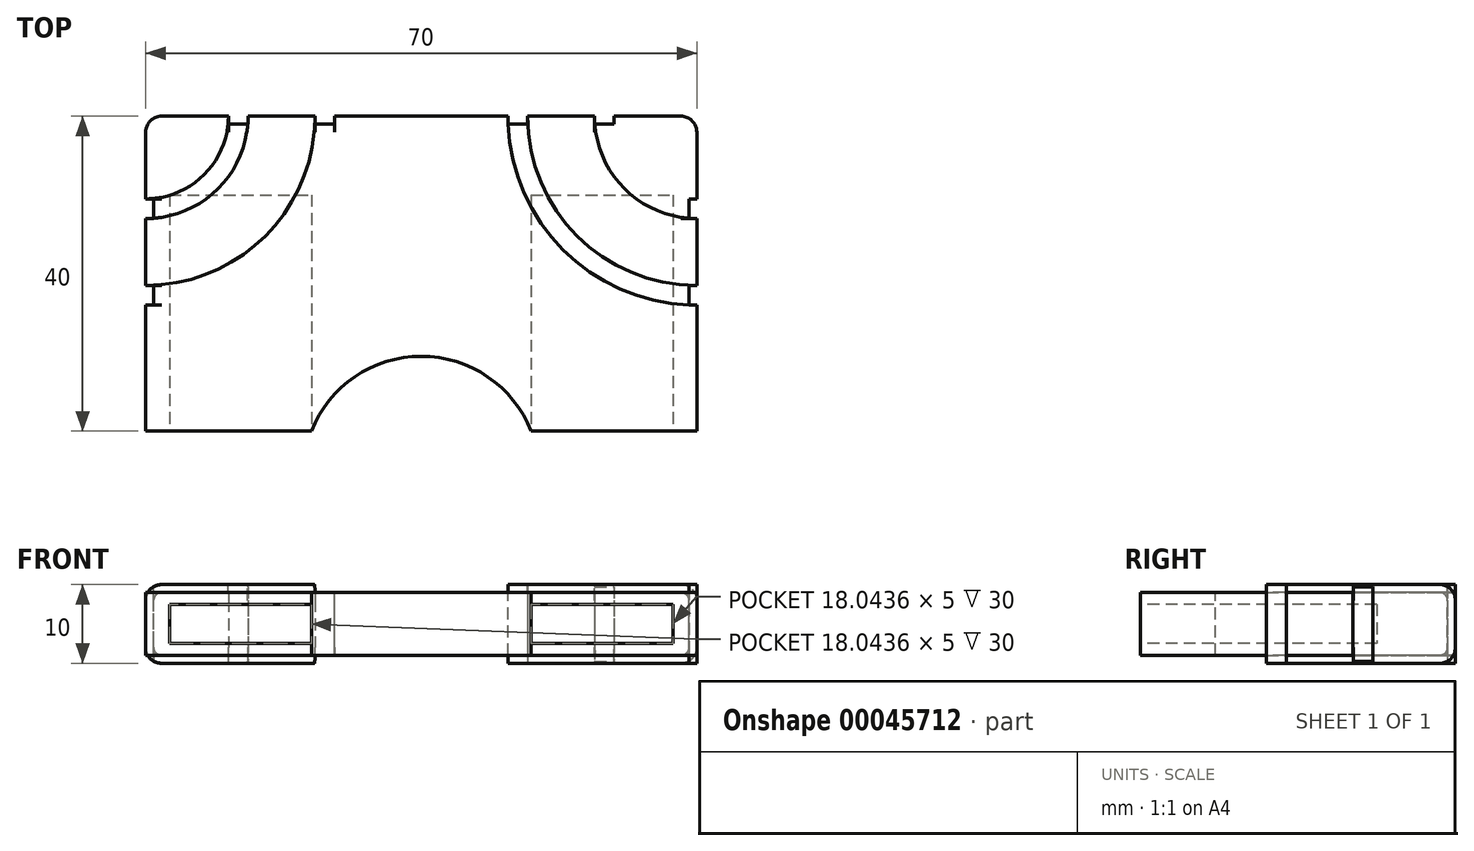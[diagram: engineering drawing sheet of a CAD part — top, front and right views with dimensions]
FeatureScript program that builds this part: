
annotation { "Feature Type Name" : "Feature", "Feature Type Description" : "" }
export const myFeature = defineFeature(function(context is Context, id is Id, definition is map)
    precondition{}
    {
        {
            var Q0;
            Q0=qCreatedBy(makeId("Top.planeOp"),FACE);
            var sketch = newSketch(context, id + "F0", { "sketchPlane" : qUnion([Q0])});
            skLineSegment(sketch, "E0.top", {"start": v(35, 70) * mm, "end": v(-35, 70) * mm});
            skLineSegment(sketch, "E0.left", {"start": v(35, 30) * mm, "end": v(35, 70) * mm});
            skLineSegment(sketch, "E0.right", {"start": v(-35, 30) * mm, "end": v(-35, 70) * mm});
            skPoint(sketch, "E0.middle", {"position": v(0, 0) * mm});
            skPoint(sketch, "E0.bottom.end.orphan", {"position": v(-35, -70) * mm});
            skPoint(sketch, "E0.bottom.start.orphan", {"position": v(35, -70) * mm});
            skPoint(sketch, "E1.center.orphan", {"position": v(0, 20.05) * mm});
            skLineSegment(sketch, "E2", {"start": v(-35, 30) * mm, "end": v(-13.96, 30) * mm});
            skArc(sketch, "E3", {"start": v(13.96, 30) * mm, "mid": v(0, 39.5) * mm, "end": v(-13.96, 30) * mm});
            skPoint(sketch, "E3.centerSnap0", {"position": v(0, 30) * mm});
            skLineSegment(sketch, "E4.trimOffspring", {"start": v(13.96, 30) * mm, "end": v(35, 30) * mm});
            skSolve(sketch);
        }
        {
            var Q0;
            Q0=makeQuery(id+"F0.imprint","IMPRINT",FACE,{"disambiguationData":[TD([[makeQuery(id+"F0.imprint","IMPRINT",EDGE,{"derivedFrom":sQuery(id+"F0.wireOp",EDGE,"E0.top")}),1.0]])]});
            extrude(context, id + "F1", {"entities" : qUnion([Q0]), "depth" : 10 * mm});
        }
        {
            var Q0;
            Q0=makeQuery(id+"F1.opExtrude","CAP_FACE",FACE,{"disambiguationData":[OSD([sQuery(id+"F0.wireOp",EDGE,"E0.top"),sQuery(id+"F0.wireOp",EDGE,"E0.left"),sQuery(id+"F0.wireOp",EDGE,"E0.right"),sQuery(id+"F0.wireOp",EDGE,"E2"),sQuery(id+"F0.wireOp",EDGE,"E3"),sQuery(id+"F0.wireOp",EDGE,"E4.trimOffspring")])],"isStart":false});
            var sketch = newSketch(context, id + "F2", { "sketchPlane" : qUnion([Q0])});
            skArc(sketch, "E5", {"start": v(21.82, 30) * mm, "mid": v(0, 47) * mm, "end": v(-21.82, 30) * mm});
            skArc(sketch, "E6", {"start": v(21.97, 30) * mm, "mid": v(0, 47.15) * mm, "end": v(-21.97, 30) * mm});
            skArc(sketch, "E7", {"start": v(23.19, 31.6) * mm, "mid": v(0, 48.75) * mm, "end": v(-23.19, 31.6) * mm});
            skArc(sketch, "E8", {"start": v(23.3, 31.75) * mm, "mid": v(0, 48.9) * mm, "end": v(-23.3, 31.75) * mm});
            skLineSegment(sketch, "E9", {"start": v(-35, 31.6) * mm, "end": v(-23.19, 31.6) * mm, "construction": true});
            skLineSegment(sketch, "E10", {"start": v(35, 31.6) * mm, "end": v(35, 30) * mm, "construction": true});
            skLineSegment(sketch, "E11.trimOffspring", {"start": v(21.82, 30) * mm, "end": v(21.97, 30) * mm, "construction": true});
            skLineSegment(sketch, "E12", {"start": v(-35, 31.75) * mm, "end": v(-23.3, 31.75) * mm, "construction": true});
            skLineSegment(sketch, "E13", {"start": v(35, 31.75) * mm, "end": v(35, 30) * mm, "construction": true});
            skPoint(sketch, "E14.end.orphan", {"position": v(0, 48.75) * mm});
            skPoint(sketch, "E14.start.orphan", {"position": v(0, 47.15) * mm});
            skLineSegment(sketch, "E15", {"start": v(23.19, 31.6) * mm, "end": v(35, 31.6) * mm});
            skLineSegment(sketch, "E16", {"start": v(35, 31.75) * mm, "end": v(23.3, 31.75) * mm});
            skLineSegment(sketch, "E17", {"start": v(-23.3, 31.75) * mm, "end": v(-35, 31.75) * mm});
            skLineSegment(sketch, "E18", {"start": v(-23.19, 31.6) * mm, "end": v(-35, 31.6) * mm});
            skLineSegment(sketch, "E19.trimOffspring", {"start": v(23.3, 31.75) * mm, "end": v(35, 31.75) * mm, "construction": true});
            skLineSegment(sketch, "E20.trimOffspring", {"start": v(23.19, 31.6) * mm, "end": v(35, 31.6) * mm, "construction": true});
            skSolve(sketch);
        }
        {
            var Q0;
            {var subQ0=sQuery(id+"F0.wireOp",EDGE,"E0.right");var subQ1=sQuery(id+"F0.wireOp",EDGE,"E0.left");var subQ2=sQuery(id+"F0.wireOp",EDGE,"E0.top");Q0=makeQuery(id+"F7wkAD12ZGFxRB5_1.boolean.opBoolean","SPLIT",FACE,{"disambiguationData":[TD([makeQuery(id+"F1.opExtrude","SWEPT_FACE",FACE,{"disambiguationData":[OSD([subQ2])]})])],"derivedFrom":makeQuery(id+"F1.opExtrude","CAP_FACE",FACE,{"disambiguationData":[OSD([subQ2,subQ1,subQ0,sQuery(id+"F0.wireOp",EDGE,"E2"),sQuery(id+"F0.wireOp",EDGE,"E3"),sQuery(id+"F0.wireOp",EDGE,"E4.trimOffspring")])],"isStart":false})});}
            var sketch = newSketch(context, id + "F3", { "sketchPlane" : qUnion([Q0])});
            skArc(sketch, "E21", {"start": v(-35, 46) * mm, "mid": v(-18.03, 53.03) * mm, "end": v(-11, 70) * mm});
            skArc(sketch, "E22", {"start": v(-35, 48.5) * mm, "mid": v(-19.8, 54.8) * mm, "end": v(-13.5, 70) * mm});
            skArc(sketch, "E23", {"start": v(-35, 57) * mm, "mid": v(-25.8, 60.8) * mm, "end": v(-22, 70) * mm});
            skArc(sketch, "E24", {"start": v(-35, 59.5) * mm, "mid": v(-27.58, 62.58) * mm, "end": v(-24.5, 70) * mm});
            skLineSegment(sketch, "E25", {"start": v(-35, 70) * mm, "end": v(-7.18, 70) * mm, "construction": true});
            skArc(sketch, "E26.MirrorCS", {"start": v(35, 57) * mm, "mid": v(25.8, 60.8) * mm, "end": v(22, 70) * mm});
            skArc(sketch, "E27.MirrorCS", {"start": v(35, 46) * mm, "mid": v(18.03, 53.03) * mm, "end": v(11, 70) * mm});
            skArc(sketch, "E28.MirrorCS", {"start": v(35, 48.5) * mm, "mid": v(19.8, 54.8) * mm, "end": v(13.5, 70) * mm});
            skArc(sketch, "E29.MirrorCS", {"start": v(35, 59.5) * mm, "mid": v(27.58, 62.58) * mm, "end": v(24.5, 70) * mm});
            skLineSegment(sketch, "E30", {"start": v(35, 70) * mm, "end": v(24.5, 70) * mm, "construction": true});
            skLineSegment(sketch, "E31", {"start": v(24.5, 70) * mm, "end": v(13.5, 70) * mm, "construction": true});
            skLineSegment(sketch, "E32", {"start": v(24.5, 70) * mm, "end": v(22, 70) * mm, "construction": true});
            skLineSegment(sketch, "E33", {"start": v(13.5, 70) * mm, "end": v(11, 70) * mm, "construction": true});
            skLineSegment(sketch, "E34", {"start": v(-35, 70) * mm, "end": v(-35, 59.5) * mm, "construction": true});
            skLineSegment(sketch, "E35", {"start": v(-35, 59.5) * mm, "end": v(-35, 48.5) * mm, "construction": true});
            skSolve(sketch);
        }
        {
            var Q0;
            Q0=makeQuery(id+"F1.opExtrude","SWEPT_FACE",FACE,{"disambiguationData":[OSD([sQuery(id+"F0.wireOp",EDGE,"E0.top")])]});
            var sketch = newSketch(context, id + "F4", { "sketchPlane" : qUnion([Q0])});
            skLineSegment(sketch, "E36", {"start": v(0, 0) * mm, "end": v(0, 10) * mm});
            skLineSegment(sketch, "E37", {"start": v(-35, 0) * mm, "end": v(35, 0) * mm});
            skLineSegment(sketch, "E38", {"start": v(-24.5, 0) * mm, "end": v(-24.5, 10) * mm});
            skLineSegment(sketch, "E39", {"start": v(-13.5, 0) * mm, "end": v(-13.5, 10) * mm});
            skLineSegment(sketch, "E40", {"start": v(-24.5, 7.98) * mm, "end": v(-35, 7.98) * mm, "construction": true});
            skLineSegment(sketch, "E41", {"start": v(-13.5, 2.91) * mm, "end": v(-24.5, 2.91) * mm, "construction": true});
            skLineSegment(sketch, "E42", {"start": v(-22, 0) * mm, "end": v(-22, 10) * mm});
            skLineSegment(sketch, "E43", {"start": v(-11, 10) * mm, "end": v(-11, 0) * mm});
            skLineSegment(sketch, "E44", {"start": v(-24.5, 6.44) * mm, "end": v(-22, 6.44) * mm, "construction": true});
            skLineSegment(sketch, "E45", {"start": v(-13.5, 6.86) * mm, "end": v(-11, 6.86) * mm, "construction": true});
            skLineSegment(sketch, "E46.MirrorCS", {"start": v(11, 10) * mm, "end": v(11, 0) * mm});
            skLineSegment(sketch, "E47.MirrorCS", {"start": v(13.5, 0) * mm, "end": v(13.5, 10) * mm});
            skLineSegment(sketch, "E48.MirrorCS", {"start": v(22, 0) * mm, "end": v(22, 10) * mm});
            skLineSegment(sketch, "E49.MirrorCS", {"start": v(24.5, 0) * mm, "end": v(24.5, 10) * mm});
            skSolve(sketch);
        }
        {
            var Q0;
            Q0=makeQuery(id+"F1.opExtrude","SWEPT_FACE",FACE,{"disambiguationData":[OSD([sQuery(id+"F0.wireOp",EDGE,"E0.right")])]});
            var sketch = newSketch(context, id + "F5", { "sketchPlane" : qUnion([Q0])});
            skLineSegment(sketch, "E50", {"start": v(-59.5, 10) * mm, "end": v(-59.5, 0) * mm});
            skLineSegment(sketch, "E51", {"start": v(-57, 10) * mm, "end": v(-57, 0) * mm});
            skLineSegment(sketch, "E52", {"start": v(-48.5, 10) * mm, "end": v(-48.5, 0) * mm});
            skLineSegment(sketch, "E53", {"start": v(-46, 10) * mm, "end": v(-46, 0) * mm});
            skLineSegment(sketch, "E54", {"start": v(-59.5, 2.85) * mm, "end": v(-70, 2.85) * mm, "construction": true});
            skLineSegment(sketch, "E55", {"start": v(-59.5, 6.05) * mm, "end": v(-57, 6.05) * mm, "construction": true});
            skLineSegment(sketch, "E56", {"start": v(-59.5, 1.41) * mm, "end": v(-48.5, 1.41) * mm, "construction": true});
            skLineSegment(sketch, "E57", {"start": v(-48.5, 6.71) * mm, "end": v(-46, 6.71) * mm, "construction": true});
            skSolve(sketch);
        }
        {
            var Q0;
            Q0=makeQuery(id+"F1.opExtrude","SWEPT_FACE",FACE,{"disambiguationData":[OSD([sQuery(id+"F0.wireOp",EDGE,"E0.left")])]});
            var sketch = newSketch(context, id + "F6", { "sketchPlane" : qUnion([Q0])});
            skLineSegment(sketch, "E58", {"start": v(59.5, 0) * mm, "end": v(59.5, 10) * mm});
            skLineSegment(sketch, "E59", {"start": v(57, 10) * mm, "end": v(57, 0) * mm});
            skLineSegment(sketch, "E60", {"start": v(48.5, 10) * mm, "end": v(48.5, 0) * mm});
            skLineSegment(sketch, "E61", {"start": v(46, 10) * mm, "end": v(46, 0) * mm});
            skLineSegment(sketch, "E62", {"start": v(59.5, 7.87) * mm, "end": v(70, 7.87) * mm, "construction": true});
            skLineSegment(sketch, "E63", {"start": v(57, 6.04) * mm, "end": v(59.5, 6.04) * mm, "construction": true});
            skLineSegment(sketch, "E64", {"start": v(59.5, 1.44) * mm, "end": v(48.5, 1.44) * mm, "construction": true});
            skLineSegment(sketch, "E65", {"start": v(48.5, 6.66) * mm, "end": v(46, 6.66) * mm, "construction": true});
            skSolve(sketch);
        }
        {
            var Q0;
            Q0=makeQuery(id+"F1.opExtrude","CAP_FACE",FACE,{"disambiguationData":[OSD([sQuery(id+"F0.wireOp",EDGE,"E0.top"),sQuery(id+"F0.wireOp",EDGE,"E0.left"),sQuery(id+"F0.wireOp",EDGE,"E0.right"),sQuery(id+"F0.wireOp",EDGE,"E2"),sQuery(id+"F0.wireOp",EDGE,"E3"),sQuery(id+"F0.wireOp",EDGE,"E4.trimOffspring")])],"isStart":true});
            extrude(context, id + "F7", {"entities" : qUnion([Q0]), "operationType" : NewBodyOperationType.REMOVE, "oppositeDirection" : true, "depth" : 5 * mm});
        }
        {
            var Q0;
            {var subQ0=sQuery(id+"F4.wireOp",EDGE,"E38");Q0=makeQuery(id+"F4.imprint","IMPRINT",FACE,{"disambiguationData":[TD([[makeQuery(id+"F4.imprint","IMPRINT",EDGE,{"derivedFrom":subQ0}),-1.0]])]});}
            var Q1;
            {var subQ0=sQuery(id+"F4.wireOp",EDGE,"E39");Q1=makeQuery(id+"F4.imprint","IMPRINT",FACE,{"disambiguationData":[TD([[makeQuery(id+"F4.imprint","IMPRINT",EDGE,{"derivedFrom":subQ0}),-1.0]])]});}
            var Q2;
            {var subQ0=sQuery(id+"F4.wireOp",EDGE,"E46.MirrorCS");Q2=makeQuery(id+"F4.imprint","IMPRINT",FACE,{"disambiguationData":[TD([[makeQuery(id+"F4.imprint","IMPRINT",EDGE,{"derivedFrom":subQ0}),1.0]])]});}
            var Q3;
            {var subQ0=sQuery(id+"F4.wireOp",EDGE,"E48.MirrorCS");Q3=makeQuery(id+"F4.imprint","IMPRINT",FACE,{"disambiguationData":[TD([[makeQuery(id+"F4.imprint","IMPRINT",EDGE,{"derivedFrom":subQ0}),-1.0]])]});}
            extrude(context, id + "F8", {"entities" : qUnion([Q0, Q1, Q2, Q3]), "operationType" : NewBodyOperationType.REMOVE, "oppositeDirection" : true, "depth" : 1 * mm});
        }
        {
            var Q0;
            {var subQ0=sQuery(id+"F5.wireOp",EDGE,"E50");Q0=makeQuery(id+"F5.imprint","IMPRINT",FACE,{"disambiguationData":[TD([[makeQuery(id+"F5.imprint","IMPRINT",EDGE,{"derivedFrom":subQ0}),1.0]])]});}
            var Q1;
            {var subQ0=sQuery(id+"F5.wireOp",EDGE,"E52");Q1=makeQuery(id+"F5.imprint","IMPRINT",FACE,{"disambiguationData":[TD([[makeQuery(id+"F5.imprint","IMPRINT",EDGE,{"derivedFrom":subQ0}),1.0]])]});}
            extrude(context, id + "F9", {"entities" : qUnion([Q0, Q1]), "operationType" : NewBodyOperationType.REMOVE, "oppositeDirection" : true, "depth" : 1 * mm});
        }
        {
            var Q0;
            {var subQ0=sQuery(id+"F6.wireOp",EDGE,"E60");Q0=makeQuery(id+"F6.imprint","IMPRINT",FACE,{"disambiguationData":[TD([[makeQuery(id+"F6.imprint","IMPRINT",EDGE,{"derivedFrom":subQ0}),-1.0]])]});}
            var Q1;
            {var subQ0=sQuery(id+"F6.wireOp",EDGE,"E58");Q1=makeQuery(id+"F6.imprint","IMPRINT",FACE,{"disambiguationData":[TD([[makeQuery(id+"F6.imprint","IMPRINT",EDGE,{"derivedFrom":subQ0}),1.0]])]});}
            extrude(context, id + "F10", {"entities" : qUnion([Q0, Q1]), "operationType" : NewBodyOperationType.REMOVE, "oppositeDirection" : true, "depth" : 1 * mm});
        }
        {
            var Q0;
            {var subQ0=sQuery(id+"F3.wireOp",EDGE,"E21");Q0=makeQuery(id+"F3.imprint","IMPRINT",FACE,{"disambiguationData":[TD([[makeQuery(id+"F3.imprint","IMPRINT",EDGE,{"derivedFrom":subQ0}),1.0]])]});}
            var Q1;
            {var subQ0=sQuery(id+"F3.wireOp",EDGE,"E23");Q1=makeQuery(id+"F3.imprint","IMPRINT",FACE,{"disambiguationData":[TD([[makeQuery(id+"F3.imprint","IMPRINT",EDGE,{"derivedFrom":subQ0}),1.0]])]});}
            var Q2;
            {var subQ0=sQuery(id+"F3.wireOp",EDGE,"E26.MirrorCS");Q2=makeQuery(id+"F3.imprint","IMPRINT",FACE,{"disambiguationData":[TD([[makeQuery(id+"F3.imprint","IMPRINT",EDGE,{"derivedFrom":subQ0}),-1.0]])]});}
            var Q3;
            {var subQ0=sQuery(id+"F3.wireOp",EDGE,"E27.MirrorCS");Q3=makeQuery(id+"F3.imprint","IMPRINT",FACE,{"disambiguationData":[TD([[makeQuery(id+"F3.imprint","IMPRINT",EDGE,{"derivedFrom":subQ0}),-1.0]])]});}
            extrude(context, id + "F11", {"entities" : qUnion([Q0, Q1, Q2, Q3]), "operationType" : NewBodyOperationType.REMOVE, "oppositeDirection" : true, "depth" : 1 * mm});
        }
        {
            var Q0;
            Q0=makeQuery(id+"F2.imprint","IMPRINT",FACE,{"disambiguationData":[TD([[makeQuery(id+"F2.imprint","IMPRINT",EDGE,{"derivedFrom":sQuery(id+"F2.wireOp",EDGE,"E7")}),-1.0]])]});
            var Q1;
            {var subQ0=sQuery(id+"F2.wireOp",EDGE,"E5");Q1=makeQuery(id+"F2.imprint","IMPRINT",FACE,{"disambiguationData":[TD([[makeQuery(id+"F2.imprint","IMPRINT",EDGE,{"derivedFrom":subQ0}),-1.0]])]});}
            extrude(context, id + "F12", {"entities" : qUnion([Q0, Q1]), "operationType" : NewBodyOperationType.REMOVE, "oppositeDirection" : true, "depth" : 1 * mm});
        }
        {
            var Q0;
            {var subQ0=sQuery(id+"F0.wireOp",EDGE,"E2");var subQ1=sQuery(id+"F0.wireOp",EDGE,"E0.right");var subQ3=makeQuery(id+"F9.opExtrude","SWEPT_FACE",FACE,{"disambiguationData":[OSD([sQuery(id+"F5.wireOp",EDGE,"E53")])]});Q0=makeQuery(id+"F12.boolean.opBoolean","SPLIT",EDGE,{"disambiguationData":[TD([makeQuery(id+"F9.boolean.opBoolean","COPY",FACE,{"derivedFrom":subQ3})])],"derivedFrom":makeQuery(id+"F9.boolean.opBoolean","SPLIT",EDGE,{"disambiguationData":[TD([makeQuery(id+"F1.opExtrude","SWEPT_FACE",FACE,{"disambiguationData":[OSD([subQ0])]})])],"derivedFrom":makeQuery(id+"F1.opExtrude","CAP_EDGE",EDGE,{"disambiguationData":[OSD([subQ1])],"isStart":false})})});}
            var Q1;
            {var subQ0=sQuery(id+"F0.wireOp",EDGE,"E4.trimOffspring");var subQ1=sQuery(id+"F0.wireOp",EDGE,"E0.left");var subQ4=makeQuery(id+"F10.opExtrude","SWEPT_FACE",FACE,{"disambiguationData":[OSD([sQuery(id+"F6.wireOp",EDGE,"E61")])]});Q1=makeQuery(id+"F12.boolean.opBoolean","SPLIT",EDGE,{"disambiguationData":[TD([makeQuery(id+"F10.boolean.opBoolean","COPY",FACE,{"derivedFrom":subQ4})])],"derivedFrom":makeQuery(id+"F10.boolean.opBoolean","SPLIT",EDGE,{"disambiguationData":[TD([makeQuery(id+"F1.opExtrude","SWEPT_FACE",FACE,{"disambiguationData":[OSD([subQ0])]})])],"derivedFrom":makeQuery(id+"F1.opExtrude","CAP_EDGE",EDGE,{"disambiguationData":[OSD([subQ1])],"isStart":false})})});}
            var Q2;
            {var subQ0=sQuery(id+"F0.wireOp",EDGE,"E0.left");Q2=makeQuery(id+"F10.boolean.opBoolean","SPLIT",EDGE,{"disambiguationData":[TD([makeQuery(id+"F10.opExtrude","SWEPT_FACE",FACE,{"disambiguationData":[OSD([sQuery(id+"F6.wireOp",EDGE,"E59")])]})])],"derivedFrom":makeQuery(id+"F1.opExtrude","CAP_EDGE",EDGE,{"disambiguationData":[OSD([subQ0])],"isStart":false})});}
            var Q3;
            {var subQ0=sQuery(id+"F0.wireOp",EDGE,"E0.top");var subQ1=sQuery(id+"F0.wireOp",EDGE,"E0.left");Q3=makeQuery(id+"F10.boolean.opBoolean","SPLIT",EDGE,{"disambiguationData":[TD([makeQuery(id+"F1.opExtrude","SWEPT_FACE",FACE,{"disambiguationData":[OSD([subQ0])]})])],"derivedFrom":makeQuery(id+"F1.opExtrude","CAP_EDGE",EDGE,{"disambiguationData":[OSD([subQ1])],"isStart":false})});}
            var Q4;
            {var subQ0=sQuery(id+"F0.wireOp",EDGE,"E0.top");var subQ1=sQuery(id+"F0.wireOp",EDGE,"E0.left");Q4=makeQuery(id+"F8.boolean.opBoolean","SPLIT",EDGE,{"disambiguationData":[TD([makeQuery(id+"F1.opExtrude","SWEPT_FACE",FACE,{"disambiguationData":[OSD([subQ1])]})])],"derivedFrom":makeQuery(id+"F1.opExtrude","CAP_EDGE",EDGE,{"disambiguationData":[OSD([subQ0])],"isStart":false})});}
            var Q5;
            {var subQ0=sQuery(id+"F0.wireOp",EDGE,"E0.top");Q5=makeQuery(id+"F8.boolean.opBoolean","SPLIT",EDGE,{"disambiguationData":[TD([makeQuery(id+"F8.opExtrude","SWEPT_FACE",FACE,{"disambiguationData":[OSD([sQuery(id+"F4.wireOp",EDGE,"E39")])]})])],"derivedFrom":makeQuery(id+"F1.opExtrude","CAP_EDGE",EDGE,{"disambiguationData":[OSD([subQ0])],"isStart":false})});}
            var Q6;
            {var subQ0=sQuery(id+"F0.wireOp",EDGE,"E0.top");Q6=makeQuery(id+"F8.boolean.opBoolean","SPLIT",EDGE,{"disambiguationData":[TD([makeQuery(id+"F8.opExtrude","SWEPT_FACE",FACE,{"disambiguationData":[OSD([sQuery(id+"F4.wireOp",EDGE,"E43")])]})])],"derivedFrom":makeQuery(id+"F1.opExtrude","CAP_EDGE",EDGE,{"disambiguationData":[OSD([subQ0])],"isStart":false})});}
            var Q7;
            {var subQ0=sQuery(id+"F0.wireOp",EDGE,"E0.top");Q7=makeQuery(id+"F8.boolean.opBoolean","SPLIT",EDGE,{"disambiguationData":[TD([makeQuery(id+"F8.opExtrude","SWEPT_FACE",FACE,{"disambiguationData":[OSD([sQuery(id+"F4.wireOp",EDGE,"E47.MirrorCS")])]})])],"derivedFrom":makeQuery(id+"F1.opExtrude","CAP_EDGE",EDGE,{"disambiguationData":[OSD([subQ0])],"isStart":false})});}
            var Q8;
            {var subQ0=sQuery(id+"F0.wireOp",EDGE,"E0.top");var subQ1=sQuery(id+"F0.wireOp",EDGE,"E0.right");Q8=makeQuery(id+"F8.boolean.opBoolean","SPLIT",EDGE,{"disambiguationData":[TD([makeQuery(id+"F1.opExtrude","SWEPT_FACE",FACE,{"disambiguationData":[OSD([subQ1])]})])],"derivedFrom":makeQuery(id+"F1.opExtrude","CAP_EDGE",EDGE,{"disambiguationData":[OSD([subQ0])],"isStart":false})});}
            var Q9;
            {var subQ0=sQuery(id+"F0.wireOp",EDGE,"E0.top");var subQ1=sQuery(id+"F0.wireOp",EDGE,"E0.right");Q9=makeQuery(id+"F9.boolean.opBoolean","SPLIT",EDGE,{"disambiguationData":[TD([makeQuery(id+"F1.opExtrude","SWEPT_FACE",FACE,{"disambiguationData":[OSD([subQ0])]})])],"derivedFrom":makeQuery(id+"F1.opExtrude","CAP_EDGE",EDGE,{"disambiguationData":[OSD([subQ1])],"isStart":false})});}
            var Q10;
            {var subQ0=sQuery(id+"F0.wireOp",EDGE,"E0.right");Q10=makeQuery(id+"F9.boolean.opBoolean","SPLIT",EDGE,{"disambiguationData":[TD([makeQuery(id+"F9.opExtrude","SWEPT_FACE",FACE,{"disambiguationData":[OSD([sQuery(id+"F5.wireOp",EDGE,"E51")])]})])],"derivedFrom":makeQuery(id+"F1.opExtrude","CAP_EDGE",EDGE,{"disambiguationData":[OSD([subQ0])],"isStart":false})});}
            var Q11;
            Q11=makeQuery(id+"F1.opExtrude","SWEPT_EDGE",EDGE,{"disambiguationData":[OSD([sQuery(id+"F0.wireOp",EDGE,"E0.top"),sQuery(id+"F0.wireOp",EDGE,"E0.left")])]});
            var Q12;
            Q12=makeQuery(id+"F1.opExtrude","SWEPT_EDGE",EDGE,{"disambiguationData":[OSD([sQuery(id+"F0.wireOp",EDGE,"E0.top"),sQuery(id+"F0.wireOp",EDGE,"E0.right")])]});
            fillet(context, id + "F13", {"entities" : qUnion([Q0, Q1, Q2, Q3, Q4, Q5, Q6, Q7, Q8, Q9, Q10, Q11, Q12]), "radius" : 2 * mm, "tangentPropagation" : true, "allowEdgeOverflow" : false});
        }
        {
            var Q0;
            {var subQ0=sQuery(id+"F0.wireOp",EDGE,"E0.left");Q0=makeQuery(id+"F11.boolean.opBoolean","INTERSECT",EDGE,{"derivedFrom":[makeQuery(id+"F10.boolean.opBoolean","COPY",FACE,{"derivedFrom":makeQuery(id+"F10.opExtrude","CAP_FACE",FACE,{"disambiguationData":[OSD([subQ0,sQuery(id+"F6.wireOp",EDGE,"E60"),sQuery(id+"F6.wireOp",EDGE,"E61")])],"isStart":false})}),makeQuery(id+"F11.opExtrude","CAP_FACE",FACE,{"disambiguationData":[OSD([sQuery(id+"F0.wireOp",EDGE,"E0.top"),subQ0,sQuery(id+"F3.wireOp",EDGE,"E27.MirrorCS"),sQuery(id+"F3.wireOp",EDGE,"E28.MirrorCS")])],"isStart":false})]});}
            var Q1;
            {var subQ0=sQuery(id+"F0.wireOp",EDGE,"E0.left");Q1=makeQuery(id+"F11.boolean.opBoolean","INTERSECT",EDGE,{"derivedFrom":[makeQuery(id+"F10.boolean.opBoolean","COPY",FACE,{"derivedFrom":makeQuery(id+"F10.opExtrude","CAP_FACE",FACE,{"disambiguationData":[OSD([subQ0,sQuery(id+"F6.wireOp",EDGE,"E58"),sQuery(id+"F6.wireOp",EDGE,"E59")])],"isStart":false})}),makeQuery(id+"F11.opExtrude","CAP_FACE",FACE,{"disambiguationData":[OSD([sQuery(id+"F0.wireOp",EDGE,"E0.top"),subQ0,sQuery(id+"F3.wireOp",EDGE,"E26.MirrorCS"),sQuery(id+"F3.wireOp",EDGE,"E29.MirrorCS")])],"isStart":false})]});}
            var Q2;
            {var subQ0=sQuery(id+"F0.wireOp",EDGE,"E0.top");Q2=makeQuery(id+"F11.boolean.opBoolean","INTERSECT",EDGE,{"derivedFrom":[makeQuery(id+"F8.boolean.opBoolean","COPY",FACE,{"derivedFrom":makeQuery(id+"F8.opExtrude","CAP_FACE",FACE,{"disambiguationData":[OSD([subQ0,sQuery(id+"F4.wireOp",EDGE,"E37"),sQuery(id+"F4.wireOp",EDGE,"E39"),sQuery(id+"F4.wireOp",EDGE,"E43")])],"isStart":false})}),makeQuery(id+"F11.opExtrude","CAP_FACE",FACE,{"disambiguationData":[OSD([subQ0,sQuery(id+"F0.wireOp",EDGE,"E0.left"),sQuery(id+"F3.wireOp",EDGE,"E27.MirrorCS"),sQuery(id+"F3.wireOp",EDGE,"E28.MirrorCS")])],"isStart":false})]});}
            var Q3;
            {var subQ0=sQuery(id+"F0.wireOp",EDGE,"E0.top");Q3=makeQuery(id+"F11.boolean.opBoolean","INTERSECT",EDGE,{"derivedFrom":[makeQuery(id+"F8.boolean.opBoolean","COPY",FACE,{"derivedFrom":makeQuery(id+"F8.opExtrude","CAP_FACE",FACE,{"disambiguationData":[OSD([subQ0,sQuery(id+"F4.wireOp",EDGE,"E37"),sQuery(id+"F4.wireOp",EDGE,"E38"),sQuery(id+"F4.wireOp",EDGE,"E42")])],"isStart":false})}),makeQuery(id+"F11.opExtrude","CAP_FACE",FACE,{"disambiguationData":[OSD([subQ0,sQuery(id+"F0.wireOp",EDGE,"E0.left"),sQuery(id+"F3.wireOp",EDGE,"E26.MirrorCS"),sQuery(id+"F3.wireOp",EDGE,"E29.MirrorCS")])],"isStart":false})]});}
            var Q4;
            {var subQ0=sQuery(id+"F0.wireOp",EDGE,"E0.top");Q4=makeQuery(id+"F11.boolean.opBoolean","INTERSECT",EDGE,{"derivedFrom":[makeQuery(id+"F8.boolean.opBoolean","COPY",FACE,{"derivedFrom":makeQuery(id+"F8.opExtrude","CAP_FACE",FACE,{"disambiguationData":[OSD([subQ0,sQuery(id+"F4.wireOp",EDGE,"E37"),sQuery(id+"F4.wireOp",EDGE,"E46.MirrorCS"),sQuery(id+"F4.wireOp",EDGE,"E47.MirrorCS")])],"isStart":false})}),makeQuery(id+"F11.opExtrude","CAP_FACE",FACE,{"disambiguationData":[OSD([subQ0,sQuery(id+"F0.wireOp",EDGE,"E0.right"),sQuery(id+"F3.wireOp",EDGE,"E21"),sQuery(id+"F3.wireOp",EDGE,"E22")])],"isStart":false})]});}
            var Q5;
            {var subQ0=sQuery(id+"F0.wireOp",EDGE,"E0.top");Q5=makeQuery(id+"F11.boolean.opBoolean","INTERSECT",EDGE,{"derivedFrom":[makeQuery(id+"F8.boolean.opBoolean","COPY",FACE,{"derivedFrom":makeQuery(id+"F8.opExtrude","CAP_FACE",FACE,{"disambiguationData":[OSD([subQ0,sQuery(id+"F4.wireOp",EDGE,"E37"),sQuery(id+"F4.wireOp",EDGE,"E48.MirrorCS"),sQuery(id+"F4.wireOp",EDGE,"E49.MirrorCS")])],"isStart":false})}),makeQuery(id+"F11.opExtrude","CAP_FACE",FACE,{"disambiguationData":[OSD([subQ0,sQuery(id+"F0.wireOp",EDGE,"E0.right"),sQuery(id+"F3.wireOp",EDGE,"E23"),sQuery(id+"F3.wireOp",EDGE,"E24")])],"isStart":false})]});}
            var Q6;
            {var subQ0=sQuery(id+"F0.wireOp",EDGE,"E0.right");Q6=makeQuery(id+"F11.boolean.opBoolean","INTERSECT",EDGE,{"derivedFrom":[makeQuery(id+"F9.boolean.opBoolean","COPY",FACE,{"derivedFrom":makeQuery(id+"F9.opExtrude","CAP_FACE",FACE,{"disambiguationData":[OSD([subQ0,sQuery(id+"F5.wireOp",EDGE,"E50"),sQuery(id+"F5.wireOp",EDGE,"E51")])],"isStart":false})}),makeQuery(id+"F11.opExtrude","CAP_FACE",FACE,{"disambiguationData":[OSD([sQuery(id+"F0.wireOp",EDGE,"E0.top"),subQ0,sQuery(id+"F3.wireOp",EDGE,"E23"),sQuery(id+"F3.wireOp",EDGE,"E24")])],"isStart":false})]});}
            var Q7;
            {var subQ0=sQuery(id+"F0.wireOp",EDGE,"E0.right");Q7=makeQuery(id+"F11.boolean.opBoolean","INTERSECT",EDGE,{"derivedFrom":[makeQuery(id+"F9.boolean.opBoolean","COPY",FACE,{"derivedFrom":makeQuery(id+"F9.opExtrude","CAP_FACE",FACE,{"disambiguationData":[OSD([subQ0,sQuery(id+"F5.wireOp",EDGE,"E52"),sQuery(id+"F5.wireOp",EDGE,"E53")])],"isStart":false})}),makeQuery(id+"F11.opExtrude","CAP_FACE",FACE,{"disambiguationData":[OSD([sQuery(id+"F0.wireOp",EDGE,"E0.top"),subQ0,sQuery(id+"F3.wireOp",EDGE,"E21"),sQuery(id+"F3.wireOp",EDGE,"E22")])],"isStart":false})]});}
            fillet(context, id + "F14", {"entities" : qUnion([Q0, Q1, Q2, Q3, Q4, Q5, Q6, Q7]), "radius" : 1 * mm, "tangentPropagation" : true, "allowEdgeOverflow" : false});
        }
        {
            var Q0;
            Q0=qCreatedBy(makeId("Top.planeOp"),FACE);
            cPlane(context, id + "F15", {"entities" : qUnion([Q0]), "cplaneType" : CPlaneType.OFFSET, "offset" : 5 * mm, "width" : 150 * mm, "height" : 150 * mm});
        }
        {
            var Q0;
            Q0=makeQuery(id+"F1.opExtrude","SWEPT_BODY",BODY,{"disambiguationData":[OSD([sQuery(id+"F0.wireOp",EDGE,"E0.top"),sQuery(id+"F0.wireOp",EDGE,"E0.left"),sQuery(id+"F0.wireOp",EDGE,"E0.right"),sQuery(id+"F0.wireOp",EDGE,"E2"),sQuery(id+"F0.wireOp",EDGE,"E3"),sQuery(id+"F0.wireOp",EDGE,"E4.trimOffspring")])]});
            var Q1;
            Q1=qCreatedBy(id+"F15.planeOp",FACE);
            mirror(context, id + "F16", {"entities" : qUnion([Q0]), "mirrorPlane" : qUnion([Q1])});
        }
        {
            var Q0;
            Q0=makeQuery(id+"F16.opPattern","COPY",BODY,{"derivedFrom":makeQuery(id+"F1.opExtrude","SWEPT_BODY",BODY,{"disambiguationData":[OSD([sQuery(id+"F0.wireOp",EDGE,"E0.top"),sQuery(id+"F0.wireOp",EDGE,"E0.left"),sQuery(id+"F0.wireOp",EDGE,"E0.right"),sQuery(id+"F0.wireOp",EDGE,"E2"),sQuery(id+"F0.wireOp",EDGE,"E3"),sQuery(id+"F0.wireOp",EDGE,"E4.trimOffspring")])]}),"instanceName":"1"});
            var Q1;
            Q1=makeQuery(id+"F1.opExtrude","SWEPT_BODY",BODY,{"disambiguationData":[OSD([sQuery(id+"F0.wireOp",EDGE,"E0.top"),sQuery(id+"F0.wireOp",EDGE,"E0.left"),sQuery(id+"F0.wireOp",EDGE,"E0.right"),sQuery(id+"F0.wireOp",EDGE,"E2"),sQuery(id+"F0.wireOp",EDGE,"E3"),sQuery(id+"F0.wireOp",EDGE,"E4.trimOffspring")])]});
            booleanBodies(context, id + "F17", {"operationType" : BooleanOperationType.UNION, "tools" : qUnion([Q0, Q1])});
        }
        {
            var Q0;
            Q0=qCreatedBy(makeId("Top.planeOp"),FACE);
            var sketch = newSketch(context, id + "F18", { "sketchPlane" : qUnion([Q0])});
            skLineSegment(sketch, "E66.bottom", {"start": v(-103.5, 62.25) * mm, "end": v(-38.83, 62.25) * mm});
            skLineSegment(sketch, "E66.top", {"start": v(-103.5, -67.75) * mm, "end": v(-38.83, -67.75) * mm});
            skLineSegment(sketch, "E66.left", {"start": v(-103.5, 62.25) * mm, "end": v(-103.5, -67.75) * mm});
            skLineSegment(sketch, "E66.right", {"start": v(-38.83, 62.25) * mm, "end": v(-38.83, -67.75) * mm});
            skSolve(sketch);
        }
        {
            var Q0;
            Q0=makeQuery(id+"F18.imprint","IMPRINT",FACE,{"disambiguationData":[TD([[makeQuery(id+"F18.imprint","IMPRINT",EDGE,{"derivedFrom":sQuery(id+"F18.wireOp",EDGE,"E66.bottom")}),-1.0]])]});
            extrude(context, id + "F19", {"entities" : qUnion([Q0]), "depth" : 6 * mm});
        }
        {
            var Q0;
            Q0=makeQuery(id+"F19.opExtrude","SWEPT_BODY",BODY,{"disambiguationData":[OSD([sQuery(id+"F18.wireOp",EDGE,"E66.bottom"),sQuery(id+"F18.wireOp",EDGE,"E66.top"),sQuery(id+"F18.wireOp",EDGE,"E66.left"),sQuery(id+"F18.wireOp",EDGE,"E66.right")])]});
            deleteBodies(context, id + "F20", {"entities" : qUnion([Q0])});
        }
        {
            var Q0;
            {var subQ0=makeQuery(id+"F1.opExtrude","SWEPT_FACE",FACE,{"disambiguationData":[OSD([sQuery(id+"F0.wireOp",EDGE,"E2")])]});Q0=makeQuery(id+"F17.opBoolean","MERGE",FACE,{"derivedFrom":[subQ0,makeQuery(id+"F16.opPattern","COPY",FACE,{"derivedFrom":subQ0,"instanceName":"1"})]});}
            var sketch = newSketch(context, id + "F21", { "sketchPlane" : qUnion([Q0])});
            skLineSegment(sketch, "E67.bottom", {"start": v(-32, 7.5) * mm, "end": v(32, 7.5) * mm});
            skLineSegment(sketch, "E67.top", {"start": v(-32, 2.5) * mm, "end": v(32, 2.5) * mm});
            skLineSegment(sketch, "E67.left", {"start": v(-32, 7.5) * mm, "end": v(-32, 2.5) * mm});
            skLineSegment(sketch, "E67.right", {"start": v(32, 7.5) * mm, "end": v(32, 2.5) * mm});
            skLineSegment(sketch, "E68.0.0", {"start": v(-33, 0) * mm, "end": v(-21.97, 0) * mm});
            skLineSegment(sketch, "E68.0.1", {"start": v(-21.97, 0) * mm, "end": v(-21.97, 1) * mm});
            skLineSegment(sketch, "E68.0.2", {"start": v(-21.97, 1) * mm, "end": v(-21.82, 1) * mm});
            skLineSegment(sketch, "E68.0.3", {"start": v(-21.82, 1) * mm, "end": v(-21.82, 0) * mm});
            skLineSegment(sketch, "E68.0.4", {"start": v(-21.82, 0) * mm, "end": v(-13.96, 0) * mm});
            skLineSegment(sketch, "E68.0.5", {"start": v(-13.96, 0) * mm, "end": v(-13.96, 10) * mm});
            skLineSegment(sketch, "E68.0.6", {"start": v(-13.96, 10) * mm, "end": v(-21.82, 10) * mm});
            skLineSegment(sketch, "E68.0.7", {"start": v(-21.82, 10) * mm, "end": v(-21.82, 9) * mm});
            skLineSegment(sketch, "E68.0.8", {"start": v(-21.82, 9) * mm, "end": v(-21.97, 9) * mm});
            skLineSegment(sketch, "E68.0.9", {"start": v(-21.97, 9) * mm, "end": v(-21.97, 10) * mm});
            skLineSegment(sketch, "E68.0.10", {"start": v(-21.97, 10) * mm, "end": v(-33, 10) * mm});
            skArc(sketch, "E68.0.11", {"start": v(-33, 10) * mm, "mid": v(-34.41, 9.41) * mm, "end": v(-35, 8) * mm});
            skLineSegment(sketch, "E68.0.12", {"start": v(-35, 8) * mm, "end": v(-35, 2) * mm});
            skArc(sketch, "E68.0.13", {"start": v(-33, 0) * mm, "mid": v(-34.41, 0.59) * mm, "end": v(-35, 2) * mm});
            skLineSegment(sketch, "E69.0.0", {"start": v(35, 2) * mm, "end": v(35, 8) * mm});
            skArc(sketch, "E69.0.1", {"start": v(35, 8) * mm, "mid": v(34.41, 9.41) * mm, "end": v(33, 10) * mm});
            skLineSegment(sketch, "E69.0.2", {"start": v(33, 10) * mm, "end": v(21.97, 10) * mm});
            skLineSegment(sketch, "E69.0.3", {"start": v(21.97, 10) * mm, "end": v(21.97, 9) * mm});
            skLineSegment(sketch, "E69.0.4", {"start": v(21.97, 9) * mm, "end": v(21.82, 9) * mm});
            skLineSegment(sketch, "E69.0.5", {"start": v(21.82, 9) * mm, "end": v(21.82, 10) * mm});
            skLineSegment(sketch, "E69.0.6", {"start": v(21.82, 10) * mm, "end": v(13.96, 10) * mm});
            skLineSegment(sketch, "E69.0.7", {"start": v(13.96, 10) * mm, "end": v(13.96, 0) * mm});
            skLineSegment(sketch, "E69.0.8", {"start": v(13.96, 0) * mm, "end": v(21.82, 0) * mm});
            skLineSegment(sketch, "E69.0.9", {"start": v(21.82, 0) * mm, "end": v(21.82, 1) * mm});
            skLineSegment(sketch, "E69.0.10", {"start": v(21.82, 1) * mm, "end": v(21.97, 1) * mm});
            skLineSegment(sketch, "E69.0.11", {"start": v(21.97, 1) * mm, "end": v(21.97, 0) * mm});
            skLineSegment(sketch, "E69.0.12", {"start": v(21.97, 0) * mm, "end": v(33, 0) * mm});
            skArc(sketch, "E69.0.13", {"start": v(35, 2) * mm, "mid": v(34.41, 0.59) * mm, "end": v(33, 0) * mm});
            skLineSegment(sketch, "E70.0.0", {"start": v(-35, 2) * mm, "end": v(-35, 8) * mm});
            skLineSegment(sketch, "E71.0.2", {"start": v(35, 8) * mm, "end": v(35, 2) * mm});
            skLineSegment(sketch, "E72", {"start": v(-32, 5) * mm, "end": v(-35, 5) * mm, "construction": true});
            skSolve(sketch);
        }
        {
            var Q0;
            {var subQ0=sQuery(id+"F21.wireOp",EDGE,"E67.left");Q0=makeQuery(id+"F21.imprint","IMPRINT",FACE,{"disambiguationData":[TD([[makeQuery(id+"F21.imprint","IMPRINT",EDGE,{"derivedFrom":subQ0}),1.0]])]});}
            var Q1;
            {var subQ0=sQuery(id+"F21.wireOp",EDGE,"E67.right");Q1=makeQuery(id+"F21.imprint","IMPRINT",FACE,{"disambiguationData":[TD([[makeQuery(id+"F21.imprint","IMPRINT",EDGE,{"derivedFrom":subQ0}),-1.0]])]});}
            extrude(context, id + "F22", {"entities" : qUnion([Q0, Q1]), "operationType" : NewBodyOperationType.REMOVE, "oppositeDirection" : true, "depth" : 30 * mm});
        }
        {
            var Q0;
            Q0=makeQuery(id+"F16.opPattern","COPY",BODY,{"derivedFrom":makeQuery(id+"F1.opExtrude","SWEPT_BODY",BODY,{"disambiguationData":[OSD([sQuery(id+"F0.wireOp",EDGE,"E0.top"),sQuery(id+"F0.wireOp",EDGE,"E0.left"),sQuery(id+"F0.wireOp",EDGE,"E0.right"),sQuery(id+"F0.wireOp",EDGE,"E2"),sQuery(id+"F0.wireOp",EDGE,"E3"),sQuery(id+"F0.wireOp",EDGE,"E4.trimOffspring")])]}),"instanceName":"1"});
            var Q1;
            Q1=qCreatedBy(makeId("Front.planeOp"),FACE);
            mirror(context, id + "F23", {"operationType" : NewBodyOperationType.ADD, "entities" : qUnion([Q0]), "mirrorPlane" : qUnion([Q1])});
        }
        {
            var Q0;
            Q0=makeQuery(id+"F23.opPattern","COPY",BODY,{"derivedFrom":makeQuery(id+"F16.opPattern","COPY",BODY,{"derivedFrom":makeQuery(id+"F1.opExtrude","SWEPT_BODY",BODY,{"disambiguationData":[OSD([sQuery(id+"F0.wireOp",EDGE,"E0.top"),sQuery(id+"F0.wireOp",EDGE,"E0.left"),sQuery(id+"F0.wireOp",EDGE,"E0.right"),sQuery(id+"F0.wireOp",EDGE,"E2"),sQuery(id+"F0.wireOp",EDGE,"E3"),sQuery(id+"F0.wireOp",EDGE,"E4.trimOffspring")])]}),"instanceName":"1"}),"instanceName":"1"});
            deleteBodies(context, id + "F24", {"entities" : qUnion([Q0])});
        }
    });
